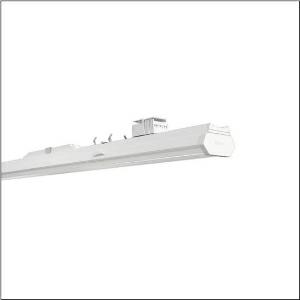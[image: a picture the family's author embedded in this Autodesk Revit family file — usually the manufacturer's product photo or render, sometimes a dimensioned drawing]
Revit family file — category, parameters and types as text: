
# Revit family: licross_21_protected_mo_52tp12dn48xg
name_source: partatom
category: Lighting Fixtures
units: mm (PartAtom-declared; Revit-internal decimal feet)

## family parameters
Cut with Voids When Loaded = No
Host = Face
Light Source = No
Part Type = Normal
Room Calculation Point = No
Round Connector Dimension = Use Diameter
Shared = No

## types (1)
- --- (1 x LED, 8000 lm, 45.3 W, 4000K)
    Apparent Load = 45 VA
    CIE Flux Codes = 73 92 98 99 100
    Color Rendering = 80
    Color Temperature = 4000K
    Default Elevation = 1800 mm
    Description = Licross 21 Protected MO, luminaire insert, of sheet steel, galvanised, coil coated, white, length: 1.500mm, width: 90mm, height: 103mm, LED rated luminous flux: 8.000lm, light colour: 840, SDCM (Standard Deviation of Colour Matching)MacAdam ≤ 3 SDCM (initial), control gear: DALI 2, with plug, 5-pole, with phase selection, mains connection: 220..240V, AC, 50/60Hz, rated input power: 45W, internal wiring halogen-free, primary light control with lens, of plastic, primary optical cover: cover, of PMMA, light emission: direct distribution, primary light characteristic: symmetric, protection rating (complete): IP64, insulation class (complete): insulation class I (protective earthing), certification: CE, ENEC, VDE, UKCA, protection symbol: D if used in an environment with conductive dust loads with corresponding accessories, impact resistance: IK06, permissible ambient temperature for indoor applications: -25..+45°C, corresponds to IFS (International Featured Standards) requirements for safety and quality in the food industry, reducing of maximum allowable ambient temperature of 5°C with ceiling mounting, LABS conformity tested according to VDMA 24364:2018-05, The light source and the operating device comply with the requirements of the Ecodesign Regulation (EU) 2019/2020 and are replaceable in accordance with this regulation, packaging unit: 1 piece
    Height = 92 mm
    Lamp = 1 x LED
    Lamp Light Flux = 8000 lm
    Lamp Power = 45.3 W
    Lamp count = 1
    Length = 1500 mm
    Luminous efficacy = 177 lm/W
    Manufacturer = Siteco
    ModVariant = No
    Model = 52TP12DN48XG
    Mounting Place = Ceiling
    Mounting Type = Pendant
    Number of Poles = 1
    OnlyDefault = Yes
    Power Factor = 1
    Product Name = Licross 21 Protected MO
    Product group = luminaire insert | ceiling pendant
    ProductGroupID = 901
    Protection Class = Protection class I
    Protection Degree = IP 64
    RLX_Detail_Level = 1
    RLX_Emergency_Light_Flux = 0 lm
    RLX_Emergency_Type = 0
    RLX_Emergency_Type_DB = No
    RlxData = <blob elided: 24633 chars, md5=d5913e3f>
    Socket = socket
    Standby Power = 0 W
    System Light Flux = 8000 lm
    System Power = 45 W
    Type Comments = factory setting: luminous flux: 100 % | dim-lin: 254 | 305 mA
    Type Image = l_1256148.jpg
    URL = http://relux.com
    VarID = @adj_128803
    Voltage = 0 V
    Weight = 0.00 kg
    Width = 88 mm

## geometry (parser evidence)
native form markers: Blend x4, Sweep x9
no freeform markers — native parametric forms only
